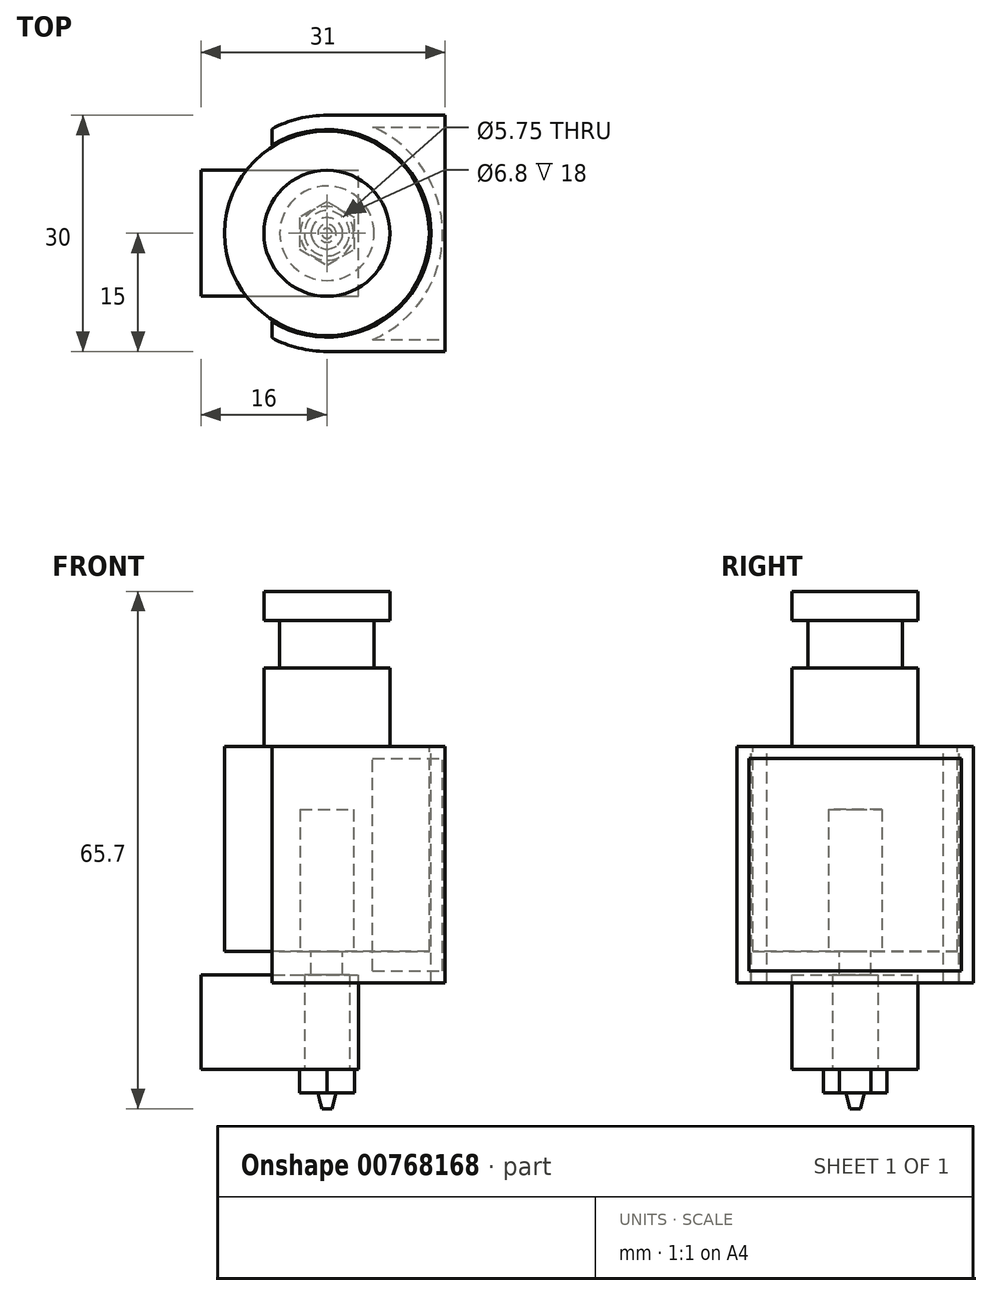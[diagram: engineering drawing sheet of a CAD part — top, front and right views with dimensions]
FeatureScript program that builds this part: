
annotation { "Feature Type Name" : "Feature", "Feature Type Description" : "" }
export const myFeature = defineFeature(function(context is Context, id is Id, definition is map)
    precondition{}
    {
        {
            var Q0;
            Q0=qCreatedBy(makeId("Top.planeOp"),FACE);
            var sketch = newSketch(context, id + "F0", { "sketchPlane" : qUnion([Q0])});
            skCircle(sketch, "E0", {"center": v(0, 0) * mm, "radius": 8 * mm});
            skSolve(sketch);
        }
        {
            var Q0;
            Q0=qSketchRegion(id+"F0",true);
            extrude(context, id + "F1", {"entities" : qUnion([Q0]), "depth" : 3.7 * mm});
        }
        {
            var Q0;
            Q0=makeQuery(id+"F1.opExtrude","CAP_FACE",FACE,{"disambiguationData":[OSD([sQuery(id+"F0.wireOp",EDGE,"E0")])],"isStart":true});
            var sketch = newSketch(context, id + "F2", { "sketchPlane" : qUnion([Q0])});
            skCircle(sketch, "E1", {"center": v(0, 0) * mm, "radius": 6 * mm});
            skSolve(sketch);
        }
        {
            var Q0;
            Q0=qSketchRegion(id+"F2",true);
            extrude(context, id + "F3", {"entities" : qUnion([Q0]), "operationType" : NewBodyOperationType.ADD, "depth" : 6 * mm});
        }
        {
            var Q0;
            Q0=makeQuery(id+"F3.opExtrude","CAP_FACE",FACE,{"disambiguationData":[OSD([sQuery(id+"F2.wireOp",EDGE,"E1")])],"isStart":false});
            var sketch = newSketch(context, id + "F4", { "sketchPlane" : qUnion([Q0])});
            skCircle(sketch, "E2", {"center": v(0, 0) * mm, "radius": 8 * mm});
            skSolve(sketch);
        }
        {
            var Q0;
            Q0=qSketchRegion(id+"F4",true);
            extrude(context, id + "F5", {"entities" : qUnion([Q0]), "operationType" : NewBodyOperationType.ADD, "depth" : (3 + 7) * mm, "offsetDistance" : 25 * mm});
        }
        {
            var Q0;
            Q0=makeQuery(id+"F5.opExtrude","CAP_FACE",FACE,{"disambiguationData":[OSD([sQuery(id+"F4.wireOp",EDGE,"E2")])],"isStart":false});
            var sketch = newSketch(context, id + "F6", { "sketchPlane" : qUnion([Q0])});
            skCircle(sketch, "E3", {"center": v(0, 0) * mm, "radius": 13 * mm});
            skSolve(sketch);
        }
        {
            var Q0;
            Q0=qSketchRegion(id+"F6",true);
            extrude(context, id + "F7", {"entities" : qUnion([Q0]), "operationType" : NewBodyOperationType.ADD, "depth" : 26 * mm, "offsetDistance" : 25 * mm});
        }
        {
            var Q0;
            Q0=makeQuery(id+"F7.opExtrude","CAP_FACE",FACE,{"disambiguationData":[OSD([sQuery(id+"F6.wireOp",EDGE,"E3")])],"isStart":false});
            var sketch = newSketch(context, id + "F8", { "sketchPlane" : qUnion([Q0])});
            skCircle(sketch, "E4", {"center": v(0, 0) * mm, "radius": 3.4 * mm});
            skSolve(sketch);
        }
        {
            var Q0;
            Q0 = qSketchRegion(id + "F8", true);
            extrude(context, id + "F9", {"entities" : qUnion([Q0]), "operationType" : NewBodyOperationType.REMOVE, "oppositeDirection" : true, "depth" : 18 * mm, "offsetDistance" : 25 * mm});
        }
        {
            var Q0;
            Q0=makeQuery(id+"F7.opExtrude","CAP_FACE",FACE,{"disambiguationData":[OSD([sQuery(id+"F6.wireOp",EDGE,"E3")])],"isStart":false});
            var sketch = newSketch(context, id + "F10", { "sketchPlane" : qUnion([Q0])});
            skCircle(sketch, "E5", {"center": v(0, 0) * mm, "radius": 3.4 * mm});
            skSolve(sketch);
        }
        {
            var Q0;
            Q0 = qSketchRegion(id + "F10", true);
            extrude(context, id + "F11", {"entities" : qUnion([Q0]), "oppositeDirection" : true, "depth" : 18 * mm, "offsetDistance" : 25 * mm});
        }
        {
            var Q0;
            Q0=makeQuery(id+"F11.opExtrude","CAP_FACE",FACE,{"disambiguationData":[OSD([sQuery(id+"F10.wireOp",EDGE,"E5")])],"isStart":true});
            var sketch = newSketch(context, id + "F12", { "sketchPlane" : qUnion([Q0])});
            skCircle(sketch, "E6", {"center": v(0, 0) * mm, "radius": 2 * mm});
            skSolve(sketch);
        }
        {
            var Q0;
            Q0 = qSketchRegion(id + "F12", true);
            extrude(context, id + "F13", {"entities" : qUnion([Q0]), "operationType" : NewBodyOperationType.ADD, "depth" : 3 * mm, "offsetDistance" : 25 * mm});
        }
        {
            var Q0;
            Q0=makeQuery(id+"F13.opExtrude","CAP_FACE",FACE,{"disambiguationData":[OSD([sQuery(id+"F12.wireOp",EDGE,"E6")])],"isStart":false});
            var sketch = newSketch(context, id + "F14", { "sketchPlane" : qUnion([Q0])});
            skCircle(sketch, "E7", {"center": v(0, 0) * mm, "radius": 2.88 * mm});
            skSolve(sketch);
        }
        {
            var Q0;
            Q0 = qSketchRegion(id + "F14", true);
            extrude(context, id + "F15", {"entities" : qUnion([Q0]), "operationType" : NewBodyOperationType.ADD, "depth" : 5 * mm, "offsetDistance" : 25 * mm});
        }
        {
            var Q0;
            Q0=makeQuery(id+"F15.opExtrude","CAP_FACE",FACE,{"disambiguationData":[OSD([sQuery(id+"F14.wireOp",EDGE,"E7")])],"isStart":true});
            var sketch = newSketch(context, id + "F16", { "sketchPlane" : qUnion([Q0])});
            skLineSegment(sketch, "E8.bottom", {"start": v(-16, -8) * mm, "end": v(4, -8) * mm});
            skLineSegment(sketch, "E8.top", {"start": v(-16, 8) * mm, "end": v(4, 8) * mm});
            skLineSegment(sketch, "E8.left", {"start": v(-16, -8) * mm, "end": v(-16, 8) * mm});
            skLineSegment(sketch, "E8.right", {"start": v(4, -8) * mm, "end": v(4, 8) * mm});
            skLineSegment(sketch, "E9", {"start": v(-16, 0) * mm, "end": v(4, 0) * mm, "construction": true});
            skSolve(sketch);
        }
        {
            var Q0;
            Q0 = qSketchRegion(id + "F16", true);
            extrude(context, id + "F17", {"entities" : qUnion([Q0]), "oppositeDirection" : true, "depth" : 12 * mm, "offsetDistance" : 25 * mm});
        }
        {
            var Q0;
            Q0=makeQuery(id+"F17.opExtrude","CAP_FACE",FACE,{"disambiguationData":[OSD([sQuery(id+"F16.wireOp",EDGE,"E8.bottom"),sQuery(id+"F16.wireOp",EDGE,"E8.top"),sQuery(id+"F16.wireOp",EDGE,"E8.left"),sQuery(id+"F16.wireOp",EDGE,"E8.right"),sQuery(id+"F16.wireOp",EDGE,"HFBCL504-6D1g-G369-yvVv-FWpguWhtGj3m")])],"isStart":false});
            var sketch = newSketch(context, id + "F18", { "sketchPlane" : qUnion([Q0])});
            skCircle(sketch, "E10", {"center": v(0, 0) * mm, "radius": 2.88 * mm});
            skSolve(sketch);
        }
        {
            var Q0;
            Q0 = qSketchRegion(id + "F18", true);
            var Q1;
            Q1=makeQuery(id+"F17.opExtrude","CAP_FACE",FACE,{"disambiguationData":[OSD([sQuery(id+"F16.wireOp",EDGE,"E8.bottom"),sQuery(id+"F16.wireOp",EDGE,"E8.top"),sQuery(id+"F16.wireOp",EDGE,"E8.left"),sQuery(id+"F16.wireOp",EDGE,"E8.right")])],"isStart":true});
            extrude(context, id + "F19", {"entities" : qUnion([Q0]), "operationType" : NewBodyOperationType.REMOVE, "endBound" : BoundingType.UP_TO_SURFACE, "oppositeDirection" : true, "depth" : 25 * mm, "endBoundEntityFace" : qUnion([Q1]), "offsetDistance" : 25 * mm});
        }
        {
            var Q0;
            Q0=makeQuery(id+"F18.imprint","IMPRINT",FACE,{"disambiguationData":[TD([[makeQuery(id+"F18.imprint","IMPRINT",EDGE,{"derivedFrom":sQuery(id+"F18.wireOp",EDGE,"E10")}),-1.0]])]});
            var sketch = newSketch(context, id + "F20", { "sketchPlane" : qUnion([Q0])});
            skCircle(sketch, "E11.cCircle", {"center": v(0, 0) * mm, "radius": 3.5 * mm, "construction": true});
            skLineSegment(sketch, "E11.0", {"start": v(-3.5, -2.02) * mm, "end": v(-3.5, 2.02) * mm});
            skLineSegment(sketch, "E11.1", {"start": v(-3.5, 2.02) * mm, "end": v(0, 4.04) * mm});
            skLineSegment(sketch, "E11.2", {"start": v(0, 4.04) * mm, "end": v(3.5, 2.02) * mm});
            skLineSegment(sketch, "E11.3", {"start": v(3.5, 2.02) * mm, "end": v(3.5, -2.02) * mm});
            skLineSegment(sketch, "E11.4", {"start": v(3.5, -2.02) * mm, "end": v(0, -4.04) * mm});
            skLineSegment(sketch, "E11.5", {"start": v(0, -4.04) * mm, "end": v(-3.5, -2.02) * mm});
            skPoint(sketch, "E11.0.midPoint", {"position": v(-3.5, 0) * mm});
            skSolve(sketch);
        }
        {
            var Q0;
            Q0 = qSketchRegion(id + "F20", true);
            extrude(context, id + "F21", {"entities" : qUnion([Q0]), "depth" : 3 * mm, "offsetDistance" : 25 * mm});
        }
        {
            var Q0;
            Q0=makeQuery(id+"F18.imprint","IMPRINT",FACE,{"disambiguationData":[TD([[makeQuery(id+"F18.imprint","IMPRINT",EDGE,{"derivedFrom":sQuery(id+"F18.wireOp",EDGE,"E10")}),-1.0]])]});
            var sketch = newSketch(context, id + "F22", { "sketchPlane" : qUnion([Q0])});
            skCircle(sketch, "E12", {"center": v(0, 0) * mm, "radius": 1.9 * mm});
            skSolve(sketch);
        }
        {
            var Q0;
            Q0=makeQuery(id+"F21.opExtrude","CAP_FACE",FACE,{"disambiguationData":[OSD([sQuery(id+"F20.wireOp",EDGE,"E11.0"),sQuery(id+"F20.wireOp",EDGE,"E11.1"),sQuery(id+"F20.wireOp",EDGE,"E11.2"),sQuery(id+"F20.wireOp",EDGE,"E11.3"),sQuery(id+"F20.wireOp",EDGE,"E11.4"),sQuery(id+"F20.wireOp",EDGE,"E11.5")])],"isStart":false});
            cPlane(context, id + "F23", {"entities" : qUnion([Q0]), "cplaneType" : CPlaneType.OFFSET, "offset" : 2 * mm, "width" : 150 * mm, "height" : 150 * mm});
        }
        {
            var Q0;
            Q0=qCreatedBy(id+"F23.planeOp",FACE);
            var sketch = newSketch(context, id + "F24", { "sketchPlane" : qUnion([Q0])});
            skCircle(sketch, "E13", {"center": v(0, 0) * mm, "radius": 0.65 * mm});
            skSolve(sketch);
        }
        {
            var Q1;
            Q1 = qSketchRegion(id + "F22", true);
            var Q2;
            Q2 = qSketchRegion(id + "F24", true);
            loft(context, id + "F25", {"operationType" : NewBodyOperationType.ADD, "sheetProfilesArray" : [{ "sheetProfileEntities" : qUnion([Q1]) }, { "sheetProfileEntities" : qUnion([Q2]) }]});
        }
        {
            var Q0;
            Q0=makeQuery(id+"F7.opExtrude","CAP_FACE",FACE,{"disambiguationData":[OSD([sQuery(id+"F6.wireOp",EDGE,"E3")])],"isStart":true});
            var sketch = newSketch(context, id + "F26", { "sketchPlane" : qUnion([Q0])});
            skArc(sketch, "E14.0", {"start": v(-7, -13.27) * mm, "mid": v(-3.6, -14.56) * mm, "end": v(0, -15) * mm});
            skLineSegment(sketch, "E15", {"start": v(-7, 13.27) * mm, "end": v(-7, 11.2) * mm});
            skCircle(sketch, "E16.0", {"center": v(0, 0) * mm, "radius": 13.2 * mm});
            skLineSegment(sketch, "E17.trimOffspring", {"start": v(-7, -11.2) * mm, "end": v(-7, -13.27) * mm});
            skLineSegment(sketch, "E18.bottom", {"start": v(0, 15) * mm, "end": v(15, 15) * mm});
            skLineSegment(sketch, "E18.top", {"start": v(0, -15) * mm, "end": v(15, -15) * mm});
            skLineSegment(sketch, "E18.right", {"start": v(15, 15) * mm, "end": v(15, -15) * mm});
            skArc(sketch, "E19.trimOffspring", {"start": v(0, 15) * mm, "mid": v(-3.6, 14.56) * mm, "end": v(-7, 13.27) * mm});
            skSolve(sketch);
        }
        {
            var Q0;
            Q0=makeQuery(id+"F26.imprint","IMPRINT",FACE,{"disambiguationData":[TD([[makeQuery(id+"F26.imprint","IMPRINT",EDGE,{"derivedFrom":sQuery(id+"F26.wireOp",EDGE,"E14.0")}),1.0]])]});
            extrude(context, id + "F27", {"entities" : qUnion([Q0]), "oppositeDirection" : true, "depth" : 30 * mm, "offsetDistance" : 25 * mm});
        }
        {
            var Q0;
            Q0=makeQuery(id+"F27.opExtrude","SWEPT_FACE",FACE,{"disambiguationData":[OSD([sQuery(id+"F26.wireOp",EDGE,"E18.right")])]});
            shell(context, id + "F28", {"entities" : qUnion([Q0]), "thickness" : 1.5 * mm});
        }
    });
